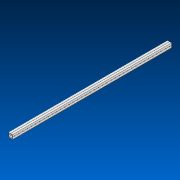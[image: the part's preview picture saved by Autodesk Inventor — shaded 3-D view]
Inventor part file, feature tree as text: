
AUTODESK INVENTOR PART (.ipt)
format: ipt  version: 2022.2 (Build 262287000, 287)  size: 819,200 bytes
history: native  units: in
note: dims shown in document units (in); Inventor stores cm internally (conversion verified against a paired STEP export)
features: other x38, extrude x1, pattern_linear x1, sketch x1, pattern_circular x1
ambient origin geometry x8: Origin, YZ Plane, XZ Plane, XY Plane, X Axis, Y Axis, Z Axis, Center Point
bodies: Solid1 (feature_tree)
feature tree (42):
  extrude  "Extrusion1"  Depth=1.0in
  other  "Work Axis1"
  pattern_linear  "Rectangular Pattern1"  Spacing1=0.0in  [1 undecoded]
  sketch  "Sketch1"  dims[d0=1.0in d1=21.0in d2=0.0in d3=14.9606in d5=1.0in]
  other  "Work Axis2"
  other  "Work Axis3"
  other  "Work Axis4"
  other  "Work Axis5"
  other  "Work Axis6"
  other  "Work Axis7"
  other  "Work Axis8"
  other  "Work Axis9"
  other  "Work Axis10"
  other  "Work Axis11"
  other  "Work Axis12"
  other  "Work Axis13"
  other  "Work Axis14"
  other  "Work Axis15"
  other  "Work Axis16"
  other  "Work Axis17"
  other  "Work Axis18"
  other  "Work Axis19"
  other  "Work Axis20"
  other  "Work Axis21"
  other  "Work Axis22"
  other  "Work Axis23"
  other  "Work Axis24"
  other  "Work Axis25"
  other  "Work Axis26"
  other  "Work Axis27"
  other  "Work Axis28"
  other  "Work Axis29"
  other  "Work Axis30"
  other  "Work Axis31"
  other  "Work Axis32"
  other  "Work Axis33"
  other  "Work Axis34"
  other  "Work Axis35"
  other  "Work Axis36"
  other  "Work Axis37"
  other  "Work Axis40"
  pattern_circular  "CirPattern2"
note: 1 required parameter value undecoded (feature->parameter linkage not recoverable at this tier; creation-order binding heuristic only, values carry confidence <= 0.55)
